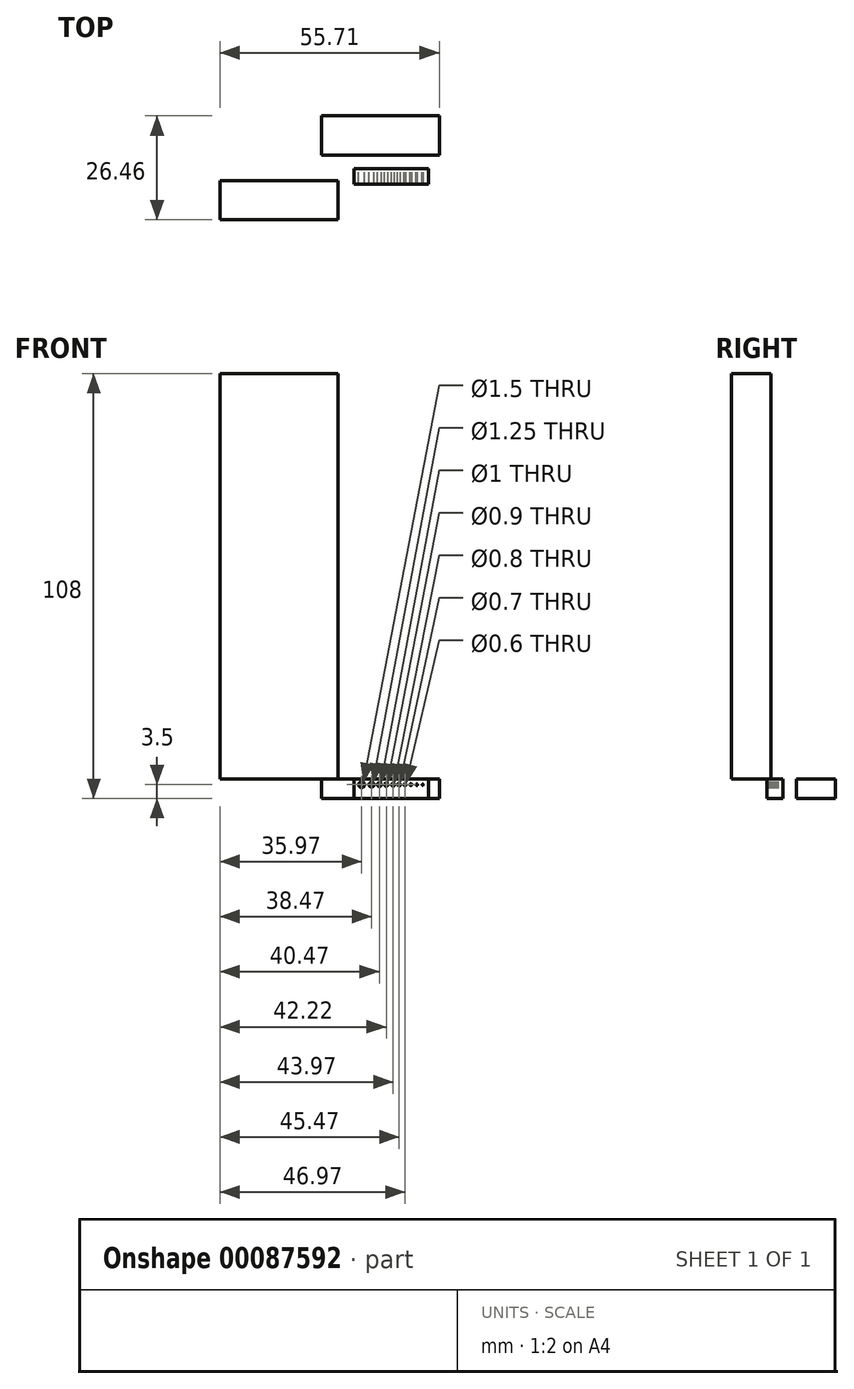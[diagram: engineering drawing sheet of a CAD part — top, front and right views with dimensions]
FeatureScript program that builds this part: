
annotation { "Feature Type Name" : "Feature", "Feature Type Description" : "" }
export const myFeature = defineFeature(function(context is Context, id is Id, definition is map)
    precondition{}
    {
        {
            var Q0;
            Q0=qCreatedBy(makeId("Front.planeOp"),FACE);
            var sketch = newSketch(context, id + "F0", { "sketchPlane" : qUnion([Q0])});
            skLineSegment(sketch, "E0.bottom", {"start": v(0, 0) * mm, "end": v(19, 0) * mm});
            skLineSegment(sketch, "E0.top", {"start": v(0, -5) * mm, "end": v(19, -5) * mm});
            skLineSegment(sketch, "E0.left", {"start": v(0, 0) * mm, "end": v(0, -5) * mm});
            skLineSegment(sketch, "E0.right", {"start": v(19, 0) * mm, "end": v(19, -5) * mm});
            skLineSegment(sketch, "E1", {"start": v(0, -1.5) * mm, "end": v(19, -1.5) * mm, "construction": true});
            skCircle(sketch, "E2", {"center": v(2, -1.5) * mm, "radius": 0.75 * mm});
            skCircle(sketch, "E3", {"center": v(4.5, -1.5) * mm, "radius": 0.62 * mm});
            skCircle(sketch, "E4", {"center": v(6.5, -1.5) * mm, "radius": 0.5 * mm});
            skCircle(sketch, "E5", {"center": v(8.25, -1.5) * mm, "radius": 0.45 * mm});
            skCircle(sketch, "E6", {"center": v(10, -1.5) * mm, "radius": 0.4 * mm});
            skCircle(sketch, "E7", {"center": v(11.5, -1.5) * mm, "radius": 0.35 * mm});
            skCircle(sketch, "E8", {"center": v(13, -1.5) * mm, "radius": 0.3 * mm});
            skCircle(sketch, "E9", {"center": v(14.5, -1.5) * mm, "radius": 0.25 * mm});
            skCircle(sketch, "E10", {"center": v(16, -1.5) * mm, "radius": 0.2 * mm});
            skCircle(sketch, "E11", {"center": v(17.5, -1.5) * mm, "radius": 0.15 * mm});
            skSolve(sketch);
        }
        {
            var Q0;
            Q0=makeQuery(id+"F0.imprint","IMPRINT",FACE,{"disambiguationData":[TD([[makeQuery(id+"F0.imprint","IMPRINT",EDGE,{"derivedFrom":sQuery(id+"F0.wireOp",EDGE,"E0.bottom")}),-1.0]])]});
            extrude(context, id + "F1", {"entities" : qUnion([Q0]), "depth" : 4 * mm});
        }
        {
            var Q0;
            Q0=qCreatedBy(makeId("Top.planeOp"),FACE);
            var sketch = newSketch(context, id + "F2", { "sketchPlane" : qUnion([Q0])});
            skLineSegment(sketch, "E12.bottom", {"start": v(-8.26, 3.39) * mm, "end": v(21.74, 3.39) * mm});
            skLineSegment(sketch, "E12.top", {"start": v(-8.26, 13.39) * mm, "end": v(21.74, 13.39) * mm});
            skLineSegment(sketch, "E12.left", {"start": v(-8.26, 3.39) * mm, "end": v(-8.26, 13.39) * mm});
            skLineSegment(sketch, "E12.right", {"start": v(21.74, 3.39) * mm, "end": v(21.74, 13.39) * mm});
            skSolve(sketch);
        }
        {
            var Q0;
            Q0=makeQuery(id+"F2.imprint","IMPRINT",FACE,{"disambiguationData":[TD([[makeQuery(id+"F2.imprint","IMPRINT",EDGE,{"derivedFrom":sQuery(id+"F2.wireOp",EDGE,"E12.bottom")}),1.0]])]});
            extrude(context, id + "F3", {"entities" : qUnion([Q0]), "oppositeDirection" : true, "depth" : 5 * mm});
        }
        {
            var Q0;
            Q0=qCreatedBy(makeId("Top.planeOp"),FACE);
            var sketch = newSketch(context, id + "F4", { "sketchPlane" : qUnion([Q0])});
            skLineSegment(sketch, "E13.bottom", {"start": v(-3.97, -3.07) * mm, "end": v(-33.97, -3.07) * mm});
            skLineSegment(sketch, "E13.top", {"start": v(-3.97, -13.07) * mm, "end": v(-33.97, -13.07) * mm});
            skLineSegment(sketch, "E13.left", {"start": v(-3.97, -3.07) * mm, "end": v(-3.97, -13.07) * mm});
            skLineSegment(sketch, "E13.right", {"start": v(-33.97, -3.07) * mm, "end": v(-33.97, -13.07) * mm});
            skSolve(sketch);
        }
        {
            var Q0;
            Q0=makeQuery(id+"F4.imprint","IMPRINT",FACE,{"disambiguationData":[TD([[makeQuery(id+"F4.imprint","IMPRINT",EDGE,{"derivedFrom":sQuery(id+"F4.wireOp",EDGE,"E13.bottom")}),1.0]])]});
            extrude(context, id + "F5", {"entities" : qUnion([Q0]), "depth" : 103 * mm});
        }
    });
